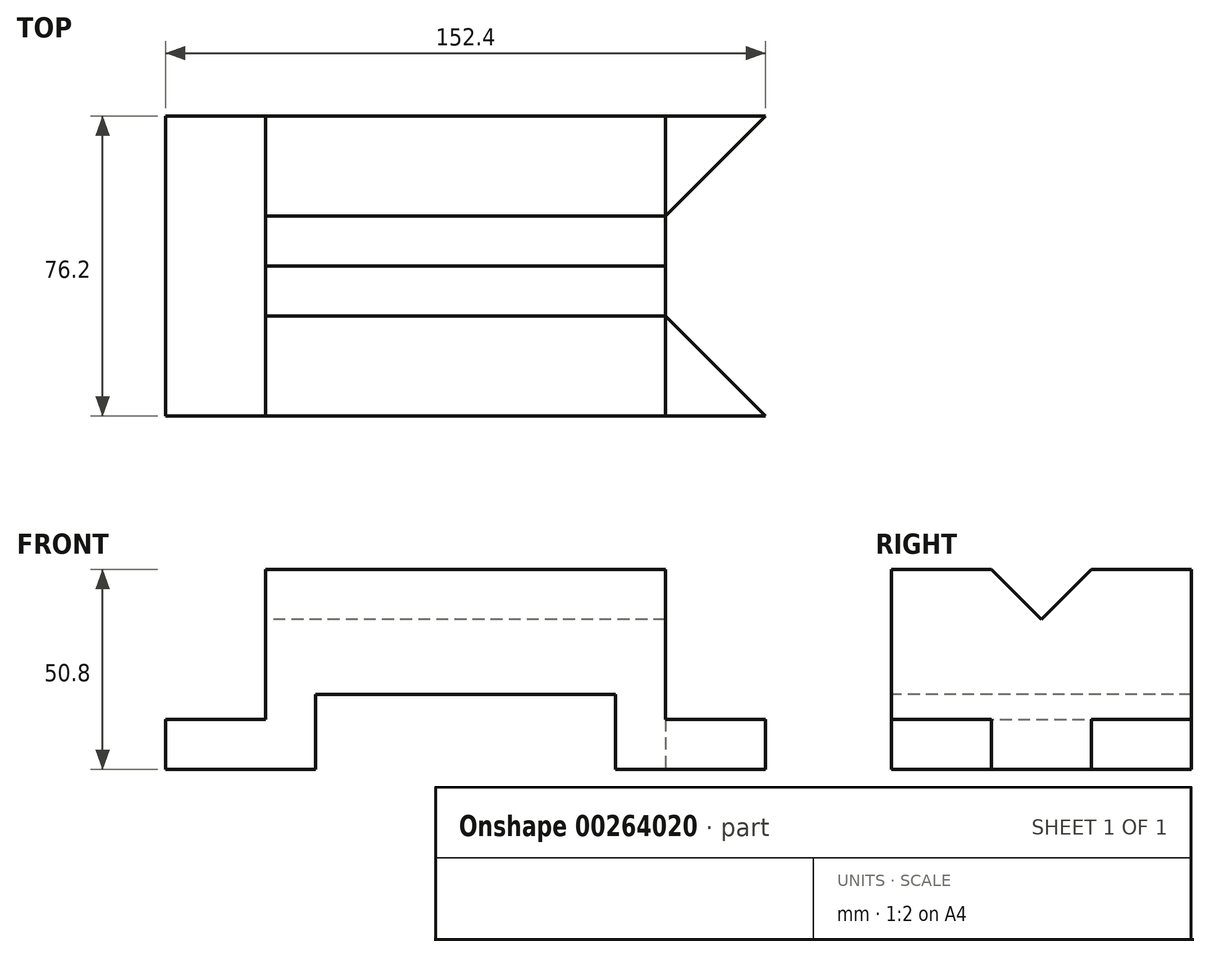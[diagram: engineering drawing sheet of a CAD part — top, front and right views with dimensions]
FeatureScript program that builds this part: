
annotation { "Feature Type Name" : "Feature", "Feature Type Description" : "" }
export const myFeature = defineFeature(function(context is Context, id is Id, definition is map)
    precondition{}
    {
        {
            var Q0;
            Q0=qCreatedBy(makeId("Right.planeOp"),FACE);
            var sketch = newSketch(context, id + "F0", { "sketchPlane" : qUnion([Q0])});
            skLineSegment(sketch, "E0", {"start": v(-40.58, 0) * mm, "end": v(35.62, 0) * mm});
            skLineSegment(sketch, "E1", {"start": v(35.62, 0) * mm, "end": v(35.62, 12.7) * mm});
            skLineSegment(sketch, "E2", {"start": v(35.62, 12.7) * mm, "end": v(10.22, 12.7) * mm});
            skLineSegment(sketch, "E3", {"start": v(10.22, 12.7) * mm, "end": v(10.22, 0) * mm});
            skLineSegment(sketch, "E4", {"start": v(-40.58, 0) * mm, "end": v(-40.58, 12.7) * mm});
            skLineSegment(sketch, "E5", {"start": v(-40.58, 12.7) * mm, "end": v(-15.18, 12.7) * mm});
            skLineSegment(sketch, "E6", {"start": v(-15.18, 12.7) * mm, "end": v(-15.18, 0) * mm});
            skLineSegment(sketch, "E7", {"start": v(-40.58, 12.7) * mm, "end": v(-40.58, 50.8) * mm});
            skLineSegment(sketch, "E8", {"start": v(35.62, 50.8) * mm, "end": v(35.62, 12.7) * mm});
            skLineSegment(sketch, "E9", {"start": v(-40.58, 50.8) * mm, "end": v(-15.18, 50.8) * mm});
            skLineSegment(sketch, "E10", {"start": v(35.62, 50.8) * mm, "end": v(10.22, 50.8) * mm});
            skLineSegment(sketch, "E11", {"start": v(10.22, 50.8) * mm, "end": v(-2.48, 38.1) * mm});
            skLineSegment(sketch, "E12", {"start": v(-15.18, 50.8) * mm, "end": v(-2.48, 38.1) * mm});
            skSolve(sketch);
        }
        {
            var Q0;
            Q0=makeQuery(id+"F0.imprint","IMPRINT",FACE,{"disambiguationData":[TD([[makeQuery(id+"F0.imprint","IMPRINT",EDGE,{"derivedFrom":sQuery(id+"F0.wireOp",EDGE,"E2")}),-1.0]])]});
            extrude(context, id + "F1", {"entities" : qUnion([Q0]), "depth" : 76.2 * mm});
        }
        {
            var Q0;
            Q0=makeQuery(id+"F1.opExtrude","CAP_FACE",FACE,{"disambiguationData":[OSD([sQuery(id+"F0.wireOp",EDGE,"E0"),sQuery(id+"F0.wireOp",EDGE,"E2"),sQuery(id+"F0.wireOp",EDGE,"E3"),sQuery(id+"F0.wireOp",EDGE,"E5"),sQuery(id+"F0.wireOp",EDGE,"E6"),sQuery(id+"F0.wireOp",EDGE,"E7"),sQuery(id+"F0.wireOp",EDGE,"E8"),sQuery(id+"F0.wireOp",EDGE,"E9"),sQuery(id+"F0.wireOp",EDGE,"E10"),sQuery(id+"F0.wireOp",EDGE,"E11"),sQuery(id+"F0.wireOp",EDGE,"E12")])],"isStart":true});
            var Q1;
            Q1=makeQuery(id+"F1.opExtrude","CAP_FACE",FACE,{"disambiguationData":[OSD([sQuery(id+"F0.wireOp",EDGE,"E0"),sQuery(id+"F0.wireOp",EDGE,"E2"),sQuery(id+"F0.wireOp",EDGE,"E3"),sQuery(id+"F0.wireOp",EDGE,"E5"),sQuery(id+"F0.wireOp",EDGE,"E6"),sQuery(id+"F0.wireOp",EDGE,"E7"),sQuery(id+"F0.wireOp",EDGE,"E8"),sQuery(id+"F0.wireOp",EDGE,"E9"),sQuery(id+"F0.wireOp",EDGE,"E10"),sQuery(id+"F0.wireOp",EDGE,"E11"),sQuery(id+"F0.wireOp",EDGE,"E12")])],"isStart":false});
            extrude(context, id + "F2", {"entities" : qUnion([Q0, Q1]), "operationType" : NewBodyOperationType.ADD, "depth" : 50.8 * mm});
        }
        {
            var Q0;
            Q0=makeQuery(id+"F1.opExtrude","CAP_FACE",FACE,{"disambiguationData":[OSD([sQuery(id+"F0.wireOp",EDGE,"E0"),sQuery(id+"F0.wireOp",EDGE,"E2"),sQuery(id+"F0.wireOp",EDGE,"E3"),sQuery(id+"F0.wireOp",EDGE,"E5"),sQuery(id+"F0.wireOp",EDGE,"E6"),sQuery(id+"F0.wireOp",EDGE,"E7"),sQuery(id+"F0.wireOp",EDGE,"E8"),sQuery(id+"F0.wireOp",EDGE,"E9"),sQuery(id+"F0.wireOp",EDGE,"E10"),sQuery(id+"F0.wireOp",EDGE,"E11"),sQuery(id+"F0.wireOp",EDGE,"E12")])],"isStart":false});
            extrude(context, id + "F3", {"entities" : qUnion([Q0]), "operationType" : NewBodyOperationType.REMOVE, "oppositeDirection" : true, "depth" : 25.4 * mm});
        }
        {
            var Q0;
            {var subQ0=sQuery(id+"F0.wireOp",EDGE,"E4");Q0=makeQuery(id+"F0.imprint","IMPRINT",FACE,{"disambiguationData":[TD([[makeQuery(id+"F0.imprint","IMPRINT",EDGE,{"derivedFrom":subQ0}),-1.0]])]});}
            extrude(context, id + "F4", {"entities" : qUnion([Q0]), "operationType" : NewBodyOperationType.ADD, "depth" : 76.2 * mm});
        }
        {
            var Q0;
            {var subQ0=sQuery(id+"F0.wireOp",EDGE,"E1");Q0=makeQuery(id+"F0.imprint","IMPRINT",FACE,{"disambiguationData":[TD([[makeQuery(id+"F0.imprint","IMPRINT",EDGE,{"derivedFrom":subQ0}),1.0]])]});}
            extrude(context, id + "F5", {"entities" : qUnion([Q0]), "operationType" : NewBodyOperationType.ADD, "depth" : 76.2 * mm});
        }
        {
            var Q0;
            {var subQ0=sQuery(id+"F0.wireOp",EDGE,"E1");Q0=makeQuery(id+"F0.imprint","IMPRINT",FACE,{"disambiguationData":[TD([[makeQuery(id+"F0.imprint","IMPRINT",EDGE,{"derivedFrom":subQ0}),1.0]])]});}
            extrude(context, id + "F6", {"entities" : qUnion([Q0]), "operationType" : NewBodyOperationType.ADD, "oppositeDirection" : true, "depth" : 76.2 * mm});
        }
        {
            var Q0;
            {var subQ0=sQuery(id+"F0.wireOp",EDGE,"E4");Q0=makeQuery(id+"F0.imprint","IMPRINT",FACE,{"disambiguationData":[TD([[makeQuery(id+"F0.imprint","IMPRINT",EDGE,{"derivedFrom":subQ0}),-1.0]])]});}
            extrude(context, id + "F7", {"entities" : qUnion([Q0]), "operationType" : NewBodyOperationType.ADD, "oppositeDirection" : true, "depth" : 76.2 * mm});
        }
        {
            var Q0;
            Q0=makeQuery(id+"F7.opExtrude","SWEPT_FACE",FACE,{"disambiguationData":[OSD([sQuery(id+"F0.wireOp",EDGE,"E6")])]});
            extrude(context, id + "F8", {"entities" : qUnion([Q0]), "operationType" : NewBodyOperationType.ADD, "depth" : 25.4 * mm});
        }
        {
            var Q0;
            {var subQ0=sQuery(id+"F0.wireOp",EDGE,"E4");var subQ1=sQuery(id+"F0.wireOp",EDGE,"E7");Q0=makeQuery(id+"F7.boolean.opBoolean","MERGE",FACE,{"derivedFrom":[makeQuery(id+"F4.boolean.opBoolean","MERGE",FACE,{"derivedFrom":[makeQuery(id+"F2.boolean.opBoolean","MERGE",FACE,{"derivedFrom":[makeQuery(id+"F1.opExtrude","SWEPT_FACE",FACE,{"disambiguationData":[OSD([subQ1])]}),makeQuery(id+"F2.opExtrude","SWEPT_FACE",FACE,{"disambiguationData":[OSD([subQ1]),TDD([makeQuery(id+"F1.opExtrude","CAP_EDGE",EDGE,{"disambiguationData":[OSD([subQ1])],"isStart":true})])]})]}),makeQuery(id+"F4.opExtrude","SWEPT_FACE",FACE,{"disambiguationData":[OSD([subQ0])]})]}),makeQuery(id+"F7.opExtrude","SWEPT_FACE",FACE,{"disambiguationData":[OSD([subQ0])]})]});}
            var sketch = newSketch(context, id + "F9", { "sketchPlane" : qUnion([Q0])});
            skLineSegment(sketch, "E13", {"start": v(-76.2, 0) * mm, "end": v(-38.1, 0) * mm});
            skLineSegment(sketch, "E14", {"start": v(-38.1, 19.05) * mm, "end": v(-38.1, 0) * mm});
            skLineSegment(sketch, "E15", {"start": v(-38.1, 19.05) * mm, "end": v(38.1, 19.05) * mm});
            skLineSegment(sketch, "E16", {"start": v(38.1, 19.05) * mm, "end": v(38.1, 0) * mm});
            skSolve(sketch);
        }
        {
            var Q0;
            {var subQ0=sQuery(id+"F9.wireOp",EDGE,"E14");Q0=makeQuery(id+"F9.imprint","IMPRINT",FACE,{"disambiguationData":[TD([[makeQuery(id+"F9.imprint","IMPRINT",EDGE,{"derivedFrom":subQ0}),1.0]])]});}
            extrude(context, id + "F10", {"entities" : qUnion([Q0]), "operationType" : NewBodyOperationType.REMOVE, "oppositeDirection" : true, "depth" : 76.2 * mm});
        }
        {
            var Q0;
            Q0=makeQuery(id+"F4.opExtrude","SWEPT_FACE",FACE,{"disambiguationData":[OSD([sQuery(id+"F0.wireOp",EDGE,"E5")])]});
            var sketch = newSketch(context, id + "F11", { "sketchPlane" : qUnion([Q0])});
            skLineSegment(sketch, "E17", {"start": v(76.2, -40.58) * mm, "end": v(50.8, -15.18) * mm});
            skLineSegment(sketch, "E18", {"start": v(50.8, -15.18) * mm, "end": v(50.8, 10.22) * mm});
            skLineSegment(sketch, "E19", {"start": v(76.2, -40.58) * mm, "end": v(76.2, 35.62) * mm});
            skPoint(sketch, "E19.endSnap0", {"position": v(76.2, -27.88) * mm});
            skLineSegment(sketch, "E20", {"start": v(76.2, 35.62) * mm, "end": v(50.8, 10.22) * mm});
            skSolve(sketch);
        }
        {
            var Q0;
            {var subQ0=sQuery(id+"F11.wireOp",EDGE,"E17");Q0=makeQuery(id+"F11.imprint","IMPRINT",FACE,{"disambiguationData":[TD([[makeQuery(id+"F11.imprint","IMPRINT",EDGE,{"derivedFrom":subQ0}),-1.0]])]});}
            extrude(context, id + "F12", {"entities" : qUnion([Q0]), "operationType" : NewBodyOperationType.REMOVE, "oppositeDirection" : true, "depth" : 12.7 * mm});
        }
        {
            var Q0;
            Q0=makeQuery(id+"F11.imprint","IMPRINT",FACE,{"disambiguationData":[TD([[makeQuery(id+"F11.imprint","IMPRINT",EDGE,{"derivedFrom":sQuery(id+"F11.wireOp",EDGE,"E18")}),-1.0]])]});
            extrude(context, id + "F13", {"entities" : qUnion([Q0]), "operationType" : NewBodyOperationType.REMOVE, "oppositeDirection" : true, "depth" : 12.7 * mm});
        }
    });
